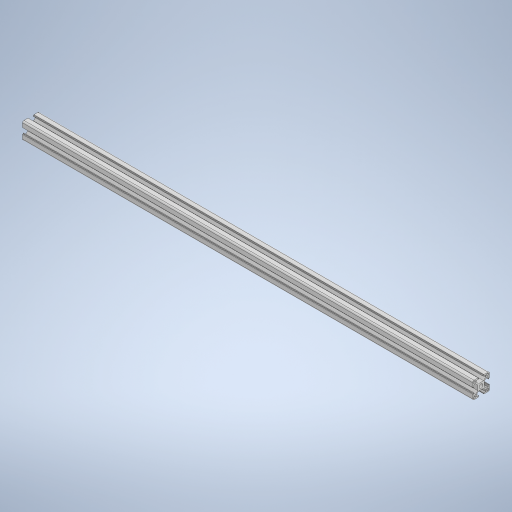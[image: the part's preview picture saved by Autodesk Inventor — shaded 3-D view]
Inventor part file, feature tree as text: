
AUTODESK INVENTOR PART (.ipt)
format: ipt  version: 2023 (Build 270158000, 158)  size: 372,224 bytes
history: native  units: mm
features: extrude x1, mirror x1, pattern_circular x1, sketch x1
ambient origin geometry x8: Origin, YZ Plane, XZ Plane, XY Plane, X Axis, Y Axis, Z Axis, Center Point
bodies: Solid1 (feature_tree)
feature tree (4):
  extrude  "Extrusion1"  TaperAngle=45.0deg  [1 undecoded]
  mirror  "Mirror1"
  pattern_circular  "Circular Pattern1"  Angle=45.0deg  [1 undecoded]
  sketch  "Sketch1"  dims[d0=3.4mm d1=45.0deg d3=45.0deg d4=2.5mm d5=135.0deg d6=1.0mm d7=4.1mm d8=5.2mm d9=8.25mm d10=15.0mm d11=2.2mm d12=5.8mm d13=1.5mm d14=1.5mm d15=1.0mm d16=1.0mm d17=1.0mm d18=800.0mm d19=0.0mm d20=40.0mm d21=360.0deg]
note: 2 required parameter values undecoded (feature->parameter linkage not recoverable at this tier; creation-order binding heuristic only, values carry confidence <= 0.55)
